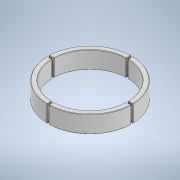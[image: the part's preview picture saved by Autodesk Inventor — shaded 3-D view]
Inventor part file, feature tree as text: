
AUTODESK INVENTOR PART (.ipt)
format: ipt  version: 2020 (Build 240168000, 168)  size: 766,464 bytes
history: native  units: mm
features: fillet x4, sketch x3, extrude x2
ambient origin geometry x8: Origin, YZ Plane, XZ Plane, XY Plane, X Axis, Y Axis, Z Axis, Center Point
bodies: Solid1 (feature_tree)
feature tree (9):
  extrude  "Extrusion1"  Depth=0.7mm
  sketch  "Sketch2"  dims[d5=0.7mm d6=0.7mm d7=0.7mm d8=0.7mm d9=0.7mm d10=0.7mm]
  extrude  "Extrusion5"  Depth=0.7mm
  fillet  "Fillet4"  Radius=0.7mm
  fillet  "Fillet5"  Radius=0.7mm
  fillet  "Fillet6"  Radius=0.7mm
  fillet  "Fillet7"  Radius=0.7mm
  sketch  "Sketch1"  dims[d0=34.5mm d1=39.0mm d2=35.2mm d3=38.3mm d4=0.7mm]
  sketch  "Sketch6"  dims[d11=0.7mm d12=3.3mm d13=0.0mm d14=34.5mm d15=39.0mm d20=34.5mm d21=39.0mm d26=34.5mm d27=39.0mm d28=0.7mm d29=7.3mm d30=0.0mm d31=0.0mm d35=3.3mm d36=0.0mm d37=0.2mm d38=0.2mm d39=0.2mm d40=0.2mm]
